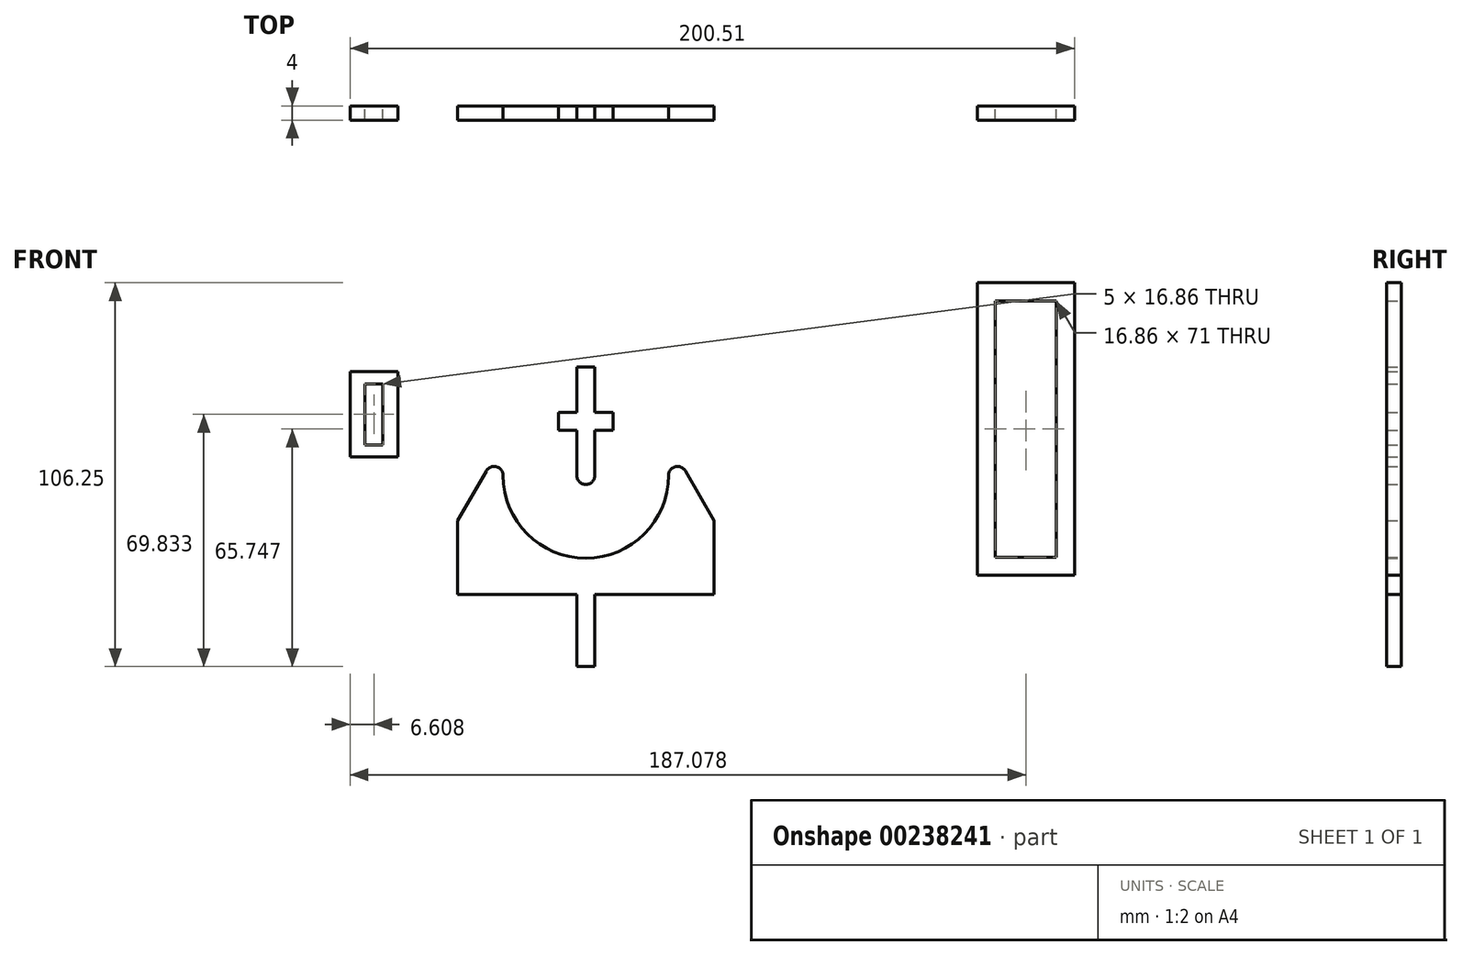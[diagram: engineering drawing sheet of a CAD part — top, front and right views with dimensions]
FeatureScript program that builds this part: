
annotation { "Feature Type Name" : "Feature", "Feature Type Description" : "" }
export const myFeature = defineFeature(function(context is Context, id is Id, definition is map)
    precondition{}
    {
        {
            var Q0;
            Q0=qCreatedBy(makeId("Front.planeOp"),FACE);
            var sketch = newSketch(context, id + "F0", { "sketchPlane" : qUnion([Q0])});
            skArc(sketch, "E0", {"start": v(-22.9, 0) * mm, "mid": v(-24.75, 2.41) * mm, "end": v(-27.57, 1.25) * mm});
            skArc(sketch, "E1", {"start": v(-22.9, 0) * mm, "mid": v(-16.2, -16.2) * mm, "end": v(0, -22.9) * mm});
            skLineSegment(sketch, "E2", {"start": v(-35.5, -32.9) * mm, "end": v(-2.5, -32.9) * mm});
            skLineSegment(sketch, "E3", {"start": v(0, -32.9) * mm, "end": v(0, -22.9) * mm, "construction": true});
            skLineSegment(sketch, "E4", {"start": v(-27.57, 1.25) * mm, "end": v(-35.5, -12.5) * mm});
            skArc(sketch, "E5.MirrorCS", {"start": v(22.9, 0) * mm, "mid": v(24.75, 2.41) * mm, "end": v(27.57, 1.25) * mm});
            skLineSegment(sketch, "E6.MirrorCS", {"start": v(27.57, 1.25) * mm, "end": v(35.5, -12.5) * mm});
            skArc(sketch, "E7.MirrorCS", {"start": v(22.9, 0) * mm, "mid": v(16.2, -16.2) * mm, "end": v(0, -22.9) * mm});
            skLineSegment(sketch, "E8.MirrorCS", {"start": v(35.5, -32.9) * mm, "end": v(2.5, -32.9) * mm});
            skArc(sketch, "E9", {"start": v(-2.5, 0) * mm, "mid": v(0, -2.5) * mm, "end": v(2.5, 0) * mm});
            skLineSegment(sketch, "E10", {"start": v(2.5, 0) * mm, "end": v(2.5, 12.5) * mm});
            skLineSegment(sketch, "E11", {"start": v(-2.5, 0) * mm, "end": v(-2.5, 12.5) * mm});
            skLineSegment(sketch, "E12", {"start": v(-2.5, 30) * mm, "end": v(2.5, 30) * mm});
            skLineSegment(sketch, "E13.bottom", {"start": v(-7.5, 12.5) * mm, "end": v(-2.5, 12.5) * mm});
            skLineSegment(sketch, "E13.top", {"start": v(-7.5, 17.5) * mm, "end": v(-2.5, 17.5) * mm});
            skLineSegment(sketch, "E13.left", {"start": v(-7.5, 12.5) * mm, "end": v(-7.5, 17.5) * mm});
            skLineSegment(sketch, "E13.right", {"start": v(7.5, 12.5) * mm, "end": v(7.5, 17.5) * mm});
            skPoint(sketch, "E13.middle", {"position": v(0, 15) * mm});
            skLineSegment(sketch, "E14.trimOffspring", {"start": v(2.5, 17.5) * mm, "end": v(7.5, 17.5) * mm});
            skLineSegment(sketch, "E15.trimOffspring", {"start": v(2.5, 17.5) * mm, "end": v(2.5, 30) * mm});
            skLineSegment(sketch, "E16.trimOffspring", {"start": v(-2.5, 17.5) * mm, "end": v(-2.5, 30) * mm});
            skLineSegment(sketch, "E17.trimOffspring", {"start": v(2.5, 12.5) * mm, "end": v(7.5, 12.5) * mm});
            skLineSegment(sketch, "E18.top", {"start": v(2.5, -52.9) * mm, "end": v(-2.5, -52.9) * mm});
            skLineSegment(sketch, "E18.left", {"start": v(2.5, -32.9) * mm, "end": v(2.5, -52.9) * mm});
            skLineSegment(sketch, "E18.right", {"start": v(-2.5, -32.9) * mm, "end": v(-2.5, -52.9) * mm});
            skPoint(sketch, "E18.middle", {"position": v(0, -42.9) * mm});
            skPoint(sketch, "E19.orphan", {"position": v(0, -32.9) * mm});
            skLineSegment(sketch, "E20", {"start": v(-35.5, -12.5) * mm, "end": v(-35.5, -32.9) * mm});
            skLineSegment(sketch, "E21", {"start": v(35.5, -12.5) * mm, "end": v(35.5, -32.9) * mm});
            skPoint(sketch, "E22.orphan", {"position": v(-47.28, -32.9) * mm});
            skPoint(sketch, "E23.orphan", {"position": v(47.28, -32.9) * mm});
            skSolve(sketch);
        }
        {
            var Q0;
            Q0=qSketchRegion(id+"F0",true);
            extrude(context, id + "F1", {"entities" : qUnion([Q0]), "depth" : 4 * mm});
        }
        {
            var Q0;
            Q0=qCreatedBy(makeId("Front.planeOp"),FACE);
            var sketch = newSketch(context, id + "F2", { "sketchPlane" : qUnion([Q0])});
            skLineSegment(sketch, "E24.bottom", {"start": v(-52.04, 5.15) * mm, "end": v(-65.25, 5.15) * mm});
            skLineSegment(sketch, "E24.top", {"start": v(-52.04, 28.72) * mm, "end": v(-65.25, 28.72) * mm});
            skLineSegment(sketch, "E24.left", {"start": v(-52.04, 5.15) * mm, "end": v(-52.04, 28.72) * mm});
            skLineSegment(sketch, "E24.right", {"start": v(-65.25, 5.15) * mm, "end": v(-65.25, 28.72) * mm});
            skPoint(sketch, "E24.middle", {"position": v(-58.64, 16.93) * mm});
            skLineSegment(sketch, "E25.bottom", {"start": v(-56.14, 8.5) * mm, "end": v(-61.14, 8.5) * mm});
            skLineSegment(sketch, "E25.top", {"start": v(-56.14, 25.36) * mm, "end": v(-61.14, 25.36) * mm});
            skLineSegment(sketch, "E25.left", {"start": v(-56.14, 8.5) * mm, "end": v(-56.14, 25.36) * mm});
            skLineSegment(sketch, "E25.right", {"start": v(-61.14, 8.5) * mm, "end": v(-61.14, 25.36) * mm});
            skLineSegment(sketch, "E26.bottom", {"start": v(135.26, 53.35) * mm, "end": v(108.4, 53.35) * mm});
            skLineSegment(sketch, "E26.top", {"start": v(135.26, -27.65) * mm, "end": v(108.4, -27.65) * mm});
            skLineSegment(sketch, "E26.left", {"start": v(135.26, 53.35) * mm, "end": v(135.26, -27.65) * mm});
            skLineSegment(sketch, "E26.right", {"start": v(108.4, 53.35) * mm, "end": v(108.4, -27.65) * mm});
            skPoint(sketch, "E26.middle", {"position": v(121.83, 12.85) * mm});
            skLineSegment(sketch, "E27.bottom", {"start": v(130.26, 48.35) * mm, "end": v(113.4, 48.35) * mm});
            skLineSegment(sketch, "E27.top", {"start": v(130.26, -22.65) * mm, "end": v(113.4, -22.65) * mm});
            skLineSegment(sketch, "E27.left", {"start": v(130.26, 48.35) * mm, "end": v(130.26, -22.65) * mm});
            skLineSegment(sketch, "E27.right", {"start": v(113.4, 48.35) * mm, "end": v(113.4, -22.65) * mm});
            skSolve(sketch);
        }
        {
            var Q0;
            Q0=makeQuery(id+"F2.imprint","IMPRINT",FACE,{"disambiguationData":[TD([[makeQuery(id+"F2.imprint","IMPRINT",EDGE,{"derivedFrom":sQuery(id+"F2.wireOp",EDGE,"E24.bottom")}),-1.0]])]});
            var Q1;
            Q1=makeQuery(id+"F2.imprint","IMPRINT",FACE,{"disambiguationData":[TD([[makeQuery(id+"F2.imprint","IMPRINT",EDGE,{"derivedFrom":sQuery(id+"F2.wireOp",EDGE,"E26.bottom")}),1.0]])]});
            extrude(context, id + "F3", {"entities" : qUnion([Q0, Q1]), "depth" : 4 * mm});
        }
    });
